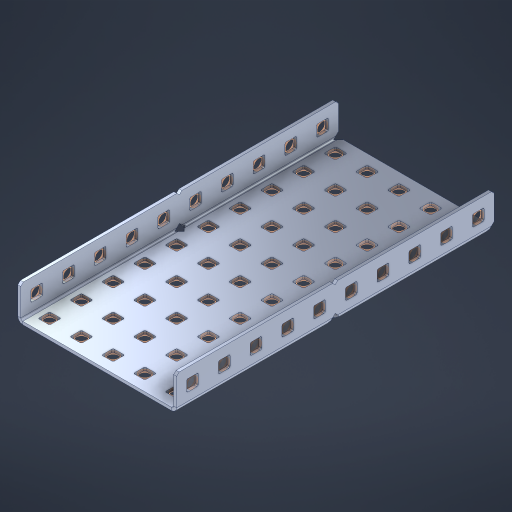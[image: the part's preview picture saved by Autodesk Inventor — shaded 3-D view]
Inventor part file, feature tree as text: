
AUTODESK INVENTOR PART (.ipt)
format: ipt  version: 2023 (Build 270158000, 158)  size: 1,043,456 bytes
history: native  units: in
note: dims shown in document units (in); Inventor stores cm internally (conversion verified against a paired STEP export)
features: other x75, extrude x69, sheet_metal_op x10, sketch x8, mirror x1, pattern_linear x1, chamfer x1
ambient origin geometry x8: Origin, YZ Plane, XZ Plane, XY Plane, X Axis, Y Axis, Z Axis, Center Point
bodies: Solid1 (feature_tree), Body (feature_tree)
feature tree (165):
  other  "Flange Pattern Plane"
  sheet_metal_op  "Flange Pattern"
  sheet_metal_op  "Body Pattern"
  other  "Arc Length"
  mirror  "Notch Mirror"
  pattern_linear  "Notch Pattern"  Spacing1=0.1875in  [1 undecoded]
  chamfer  "End Chamfer"
  extrude  "Half Cut"  Depth=0.0469in
  sketch  "Sketch1"  dims[d0=2.5in]
  other  "Plate1"
  sketch  "Sketch2"  dims[d1=5.0in]
  other  "Plate2"
  sheet_metal_op  "Bend1"
  sheet_metal_op  "Corner1"
  sketch  "Sketch3"  dims[d2=0.0469in]
  other  "Flange Pattern Sketch"
  sketch  "Sketch7"  dims[d3=0.0469in]
  other  "Srf1"
  other  "Srf2"
  sketch  "Sketch8"  dims[d4=0.0234in]
  sketch  "Sketch9"  dims[d5=0.0938in]
  other  "Srf91"
  sheet_metal_op  "Body Pattern Sketch"
  other  "Srf92"
  sketch  "Sketch13"  dims[d6=0.0469in]
  sketch  "Sketch14"  dims[d7=0.5in d8=90.0deg d9=0.0312in d10=0.1875in d11=0.0469in d12=0.0469in d16=0.182in d17=0.02in d18=0.0469in d19=0.0in d20=0.25in d21=0.25in d46=0.172in d47=1.0in d48=0.0in d49=0.182in d50=0.02in d51=0.25in d52=0.25in d53=0.0469in d54=0.0in d55=0.172in d56=1.0in d57=0.0in d60=3.937in d62=0.5in d63=1.9685in d65=0.5in d85=0.1227in d86=0.1659in d88=0.04in d89=0.0469in d90=0.0in d91=0.04in d92=0.0491in d95=2.5in d96=0.04in d97=0.25in d98=45.0deg d101=0.0in d102=2.497in d131=2.5in d132=3.937in d134=0.5in d139=0.5in]
  other  "Srf856"
  other  "Srf1310"
  other  "Srf1311"
  other  "Srf1312"
  other  "Srf1376"
  other  "Srf1377"
  other  "Srf1728"
  other  "Srf1755"
  other  "Srf1878"
  other  "Srf1879"
  other  "Srf1880"
  other  "Srf1881"
  other  "Srf1882"
  other  "Srf1883"
  other  "Srf1884"
  other  "Srf1885"
  other  "Srf1886"
  other  "Srf1887"
  other  "Srf1888"
  other  "Srf1889"
  other  "Srf1890"
  other  "Srf1891"
  other  "Srf1942"
  other  "Srf1943"
  other  "Srf1944"
  other  "Srf1945"
  other  "Srf1946"
  other  "Srf1947"
  other  "Srf1948"
  other  "Srf1949"
  other  "Srf1950"
  other  "Srf1951"
  other  "Srf1952"
  other  "Srf1953"
  other  "Srf1954"
  other  "Srf1955"
  other  "Srf1956"
  other  "Srf1957"
  other  "Srf1958"
  other  "Srf1959"
  other  "Srf1960"
  other  "Srf1961"
  other  "Srf1962"
  other  "Srf1963"
  other  "Srf1964"
  other  "Srf1965"
  other  "Srf1966"
  other  "Srf1967"
  other  "Srf1968"
  other  "Srf1969"
  other  "Srf1970"
  other  "Srf2146"
  other  "Srf2147"
  other  "Srf2148"
  other  "Srf2149"
  other  "Srf2150"
  other  "Srf2151"
  other  "Srf2152"
  other  "Srf2153"
  other  "Srf2154"
  other  "Srf2155"
  other  "Srf2156"
  other  "Srf2157"
  other  "Srf2158"
  other  "Srf2159"
  other  "Srf2160"
  sheet_metal_op  "Flange Stamp"
  sheet_metal_op  "Flange Circle"
  sheet_metal_op  "Body Stamp"
  sheet_metal_op  "Body Circle"
  sheet_metal_op  "Notch"
  extrude  "ExtrusionSrf2"  Depth=0.0469in
  extrude  "ExtrusionSrf92"  Depth=2.5in
  extrude  "ExtrusionSrf856"  Depth=0.02in
  extrude  "ExtrusionSrf1310"  Depth=0.0469in
  extrude  "ExtrusionSrf1311"  TaperAngle=0.0deg  [1 undecoded]
  extrude  "ExtrusionSrf1312"  Depth=0.25in
  extrude  "ExtrusionSrf1376"  Depth=0.25in
  extrude  "ExtrusionSrf1377"  Depth=2.5in
  extrude  "ExtrusionSrf1728"  Depth=2.5in TaperAngle=0.0deg
  extrude  "ExtrusionSrf1755"  Depth=2.5in
  extrude  "ExtrusionSrf1878"  Depth=0.02in
  extrude  "ExtrusionSrf1879"  Depth=0.25in
  extrude  "ExtrusionSrf1880"  Depth=0.25in
  extrude  "ExtrusionSrf1881"  Depth=0.0469in
  extrude  "ExtrusionSrf1882"  TaperAngle=0.0deg  [1 undecoded]
  extrude  "ExtrusionSrf1883"  Depth=2.5in
  extrude  "ExtrusionSrf1884"  Depth=2.5in TaperAngle=0.0deg
  extrude  "ExtrusionSrf1885"  Depth=2.5in
  extrude  "ExtrusionSrf1886"  Depth=2.5in
  extrude  "ExtrusionSrf1887"  Depth=2.5in
  extrude  "ExtrusionSrf1888"  Depth=2.5in
  extrude  "ExtrusionSrf1889"  Depth=2.5in
  extrude  "ExtrusionSrf1890"  Depth=0.0469in
  extrude  "ExtrusionSrf1891"  TaperAngle=0.0deg  [1 undecoded]
  extrude  "ExtrusionSrf1942"  Depth=2.5in
  extrude  "ExtrusionSrf1943"  Depth=2.5in
  extrude  "ExtrusionSrf1944"  Depth=2.5in
  extrude  "ExtrusionSrf1945"  Depth=0.25in TaperAngle=45.0deg
  extrude  "ExtrusionSrf1946"  TaperAngle=0.0deg  [1 undecoded]
  extrude  "ExtrusionSrf1947"  Depth=2.5in
  extrude  "ExtrusionSrf1948"  Depth=2.5in
  extrude  "ExtrusionSrf1949"  Depth=2.5in
  extrude  "ExtrusionSrf1950"  Depth=2.5in
  extrude  "ExtrusionSrf1951"  Depth=2.5in
  extrude  "ExtrusionSrf1952"  [1 undecoded]
  extrude  "ExtrusionSrf1953"  [1 undecoded]
  extrude  "ExtrusionSrf1954"  [1 undecoded]
  extrude  "ExtrusionSrf1955"  [1 undecoded]
  extrude  "ExtrusionSrf1956"  [1 undecoded]
  extrude  "ExtrusionSrf1957"  [1 undecoded]
  extrude  "ExtrusionSrf1958"  [1 undecoded]
  extrude  "ExtrusionSrf1959"  [1 undecoded]
  extrude  "ExtrusionSrf1960"  [1 undecoded]
  extrude  "ExtrusionSrf1961"  [1 undecoded]
  extrude  "ExtrusionSrf1962"  [1 undecoded]
  extrude  "ExtrusionSrf1963"  [1 undecoded]
  extrude  "ExtrusionSrf1964"  [1 undecoded]
  extrude  "ExtrusionSrf1965"  [1 undecoded]
  extrude  "ExtrusionSrf1966"  [1 undecoded]
  extrude  "ExtrusionSrf1967"  [1 undecoded]
  extrude  "ExtrusionSrf1968"  [1 undecoded]
  extrude  "ExtrusionSrf1969"  [1 undecoded]
  extrude  "ExtrusionSrf1970"  [1 undecoded]
  extrude  "ExtrusionSrf2146"  [1 undecoded]
  extrude  "ExtrusionSrf2147"  [1 undecoded]
  extrude  "ExtrusionSrf2148"  [1 undecoded]
  extrude  "ExtrusionSrf2149"  [1 undecoded]
  extrude  "ExtrusionSrf2150"  [1 undecoded]
  extrude  "ExtrusionSrf2151"  [1 undecoded]
  extrude  "ExtrusionSrf2152"  [1 undecoded]
  extrude  "ExtrusionSrf2153"  [1 undecoded]
  extrude  "ExtrusionSrf2154"  [1 undecoded]
  extrude  "ExtrusionSrf2155"  [1 undecoded]
  extrude  "ExtrusionSrf2156"  [1 undecoded]
  extrude  "ExtrusionSrf2157"  [1 undecoded]
  extrude  "ExtrusionSrf2158"  [1 undecoded]
  extrude  "ExtrusionSrf2159"  [1 undecoded]
  extrude  "ExtrusionSrf2160"  [1 undecoded]
note: 39 required parameter values undecoded (feature->parameter linkage not recoverable at this tier; creation-order binding heuristic only, values carry confidence <= 0.55)
